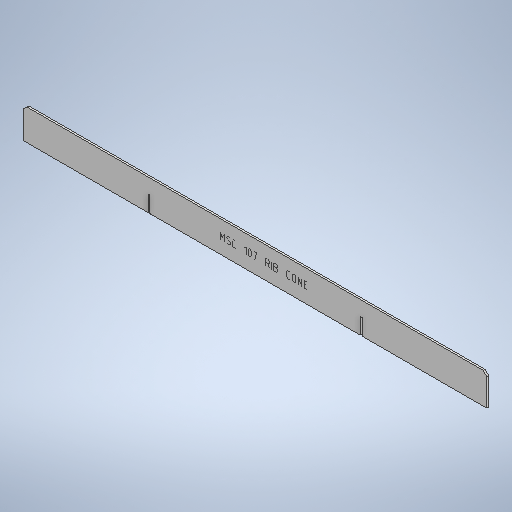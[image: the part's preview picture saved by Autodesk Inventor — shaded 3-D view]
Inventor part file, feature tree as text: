
AUTODESK INVENTOR PART (.ipt)
format: ipt  version: 2025 (Build 290162010, 162A)  size: 367,104 bytes
history: native  units: mm
features: other x5, sketch x3, sheet_metal_op x1, extrude x1
ambient origin geometry x8: Origin, YZ Plane, XZ Plane, XY Plane, X Axis, Y Axis, Z Axis, Center Point
bodies: Body1 (feature_tree)
feature tree (10):
  sheet_metal_op  "Face1"
  extrude  "Extrusion1"  Depth=50.0mm
  other  "Mark1"
  other  "A-Side Definition"
  other  "Corner Chamfer2"
  sketch  "Sketch2"  dims[d18=750.0mm d19=50.0mm]
  other  "Plate2"
  sketch  "Sketch3"  dims[d20=45.0mm]
  sketch  "Sketch5"  dims[d21=3.0mm d24=26.0mm d25=0.0mm d26=0.0mm d44=3.1mm d45=340.0mm d46=6.0mm d47=6.0mm d48=45.0deg]
  other  "Definition1"
